# Revit family: PRD_AR_WllHngWshbsns_MEDCARESingleWashbasinBarrierFree_ANMW0064
name_source: partatom
category: Plumbing Fixtures
units: mm (PartAtom-declared; Revit-internal decimal feet)

## family parameters
Cut with Voids When Loaded = Yes
Enable Cutting in Views = No
Host = Face
Maintain Annotation Orientation = No
OmniClass Number = 23.45.05.14.14
OmniClass Title = Sinks/Lavatories
Part Type = Normal
Room Calculation Point = No
Round Connector Dimension = Use Diameter
Shared = Yes

## types (1)
- ANMW0064
    AssetType = Fixed
    BIMObjectName = PRD_AR_WallHungWashbasins_MEDCARESingleWashbasinBarrierFree_ANMW0064
    BarrierFree = yes
    BowlPosition = Center
    Category = Pr_40_20_96_96, Wall-hung washbasins
    Color = alpinewhite
    Colour = alpinewhite
    ColourStrip = no
    ColourStripCheck = No
    ConnectionOffset = 137 mm  [stored 0.449475 ft]
    Default Elevation = 925 mm  [stored 3.03478 ft]
    Description = MEDCARE single washbasin made of MIRANIT resin-bonded mineral material with pore-free smooth surface (temperature-resistant up to 80 °C), Alpine white colour. Roll-under, with integrated grab rails, seamless moulded bowl, without overflow, with tap hole 35 mm (D). Mounting on washbasin back panel. Rear surge edge, including mounting material.
    DiameterNominal = 32  [stored 0.104987 ft]
    DrainSize = 32 mm  [stored 0.104987 ft]
    Export Type to IFC As = IfcSanitaryTerminalType
    Features = Alpine white colour. Roll-under, with integrated grab rails, seamless moulded bowl, without overflow, with tap hole 35 mm (D). Bowl dimensions 400 x 117 x 415 mm (W x H x D).
    Flow = 0.0 L/s
    GrabRailsCheck = Yes
    IfcExportAs = ifcSanitaryTerminalType
    IfcExportType = WASHHANDBASIN
    Manufacturer = KWC Group Management AG
    ManufacturerName = KWC Group Management AG
    ManufacturerURL = www.kwc-professional.com
    Material = mineral material
    MaterialCode = Miranit
    Model = ANMW0064
    ModelNumber = 3600015210
    ModelReference = ANMW0064
    Mounting = WALLHUNG
    MountingOffset = 0 mm  [stored 0 ft]
    NBSDescription = Wall hung wash basins
    NBSReference = 45-35-70/369
    Name = MEDCARE Single washbasin barrier-free ANMW0064
    NominalDepth = 550 mm
    NominalHeight = 150 mm
    NominalWidth = 600 mm  [stored 1.9685 ft]
    NumberOfBowls = 1
    NumberOfTapHoles = 1
    OverallDepth = 550 mm
    OverallHeight = 150 mm
    OverallWidth = 600 mm  [stored 1.9685 ft]
    Overflow = no
    OverflowCheck = No
    ProductInformation = http://pim.kwc.com
    RearUpstand = yes
    Shape = Rectangle
    SinkMaterial = PRD_AR_MineralMaterial_Alpinewhite
    SiphonDiameter = DN 32
    SiphonIncluded = no
    Size = 600 x 150 x 550 mm (W x H x D)
    Splashback = no
    Status = New
    TapHoleCheck = Yes
    TapHoleDiameter = 35 mm
    TapHolePosition = middle
    TapLedge = yes
    Type IFC Predefined Type = WASHHANDBASIN
    TypeOfBasin = Washbasin
    TypeOfMounting = wall mounting
    URL = www.kwc-professional.com
    Uniclass2015Code = Pr_40_20_96_96
    Uniclass2015Title = Wall-hung washbasins
    Uniclass2015Version = Products v1.36
    Version = 1
    WashHandBasinType = OTHER
    WasteHolePosition = centre back
    WasteSleeveIncluded = no

note: [stored X ft] marks values corroborated as IEEE doubles in the binary element streams (Revit-internal decimal feet)

## geometry (parser evidence)
native form markers: Sweep x6
no freeform markers — native parametric forms only
